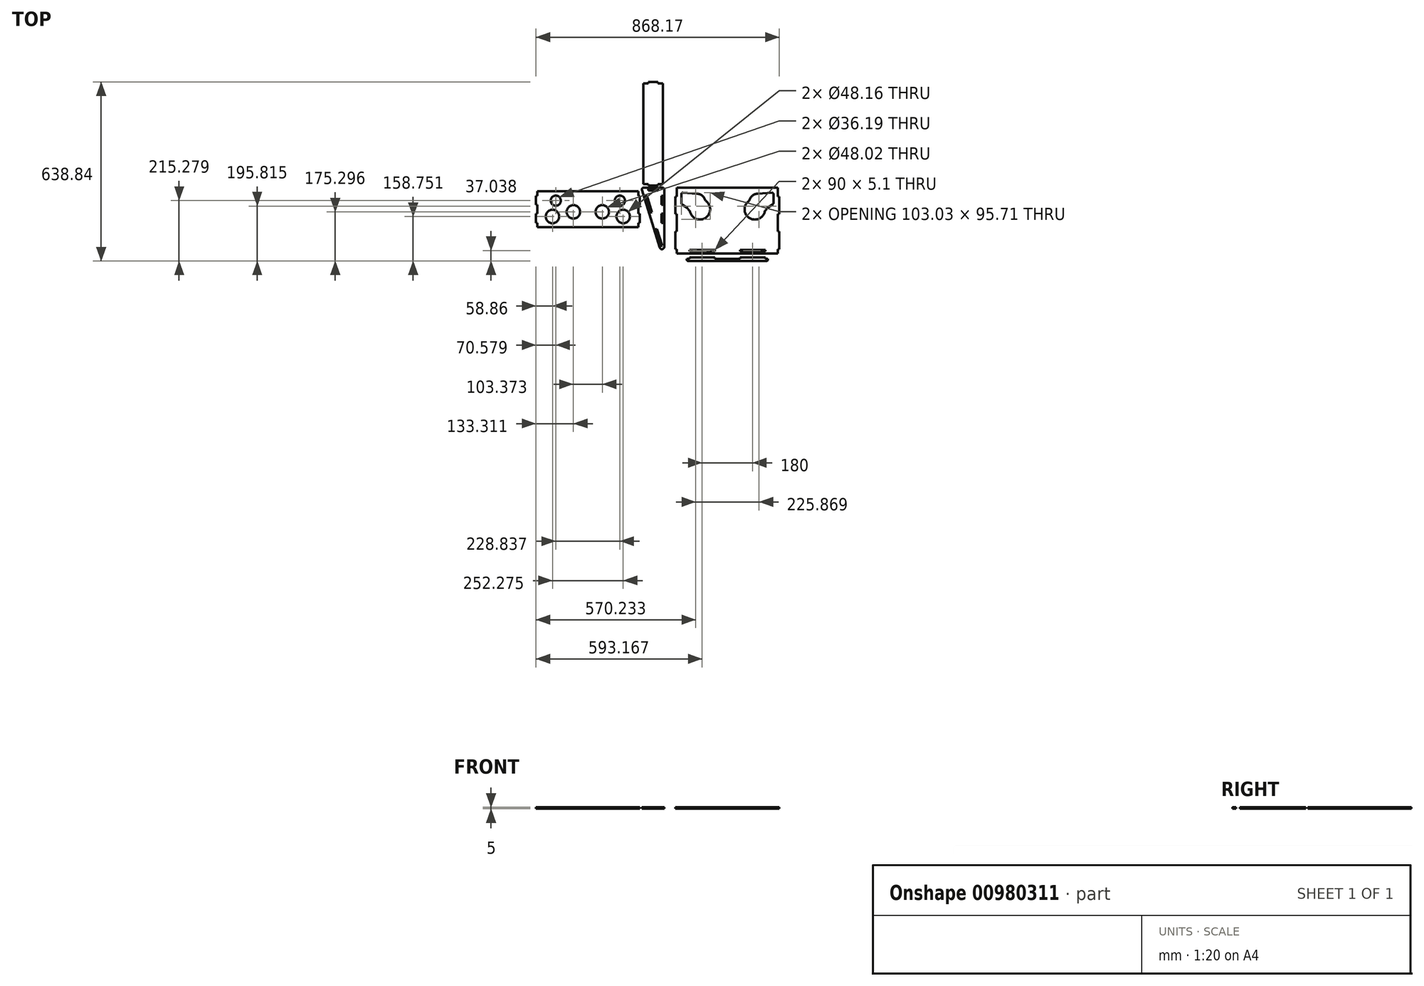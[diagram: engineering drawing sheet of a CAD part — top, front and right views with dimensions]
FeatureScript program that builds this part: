
annotation { "Feature Type Name" : "Feature", "Feature Type Description" : "" }
export const myFeature = defineFeature(function(context is Context, id is Id, definition is map)
    precondition{}
    {
        {
            var Q0;
            Q0=qCreatedBy(makeId("Top.planeOp"),FACE);
            var sketch = newSketch(context, id + "F0", { "sketchPlane" : qUnion([Q0])});
            skLineSegment(sketch, "E0.1", {"start": v(-213.88, 114.6) * mm, "end": v(-213.88, 52.1) * mm});
            skLineSegment(sketch, "E1.0", {"start": v(-208.88, 145.84) * mm, "end": v(151.12, 145.84) * mm});
            skLineSegment(sketch, "E1.1", {"start": v(-208.88, 145.84) * mm, "end": v(-208.88, 114.6) * mm});
            skLineSegment(sketch, "E1.3", {"start": v(151.12, 145.84) * mm, "end": v(151.12, 114.6) * mm});
            skLineSegment(sketch, "E2", {"start": v(-208.88, 20.84) * mm, "end": v(-208.88, 52.1) * mm});
            skLineSegment(sketch, "E3", {"start": v(-208.88, 114.6) * mm, "end": v(-208.88, 145.84) * mm});
            skLineSegment(sketch, "E4", {"start": v(-208.88, 114.6) * mm, "end": v(-213.88, 114.6) * mm});
            skLineSegment(sketch, "E5.MirrorCS", {"start": v(-208.88, 52.1) * mm, "end": v(-213.88, 52.1) * mm});
            skLineSegment(sketch, "E6.MirrorCS", {"start": v(-208.88, -10.4) * mm, "end": v(-213.88, -10.4) * mm});
            skLineSegment(sketch, "E7.MirrorCS", {"start": v(-208.88, -72.9) * mm, "end": v(-213.88, -72.9) * mm});
            skLineSegment(sketch, "E8.trimOffspring", {"start": v(-213.88, -10.4) * mm, "end": v(-213.88, -72.9) * mm});
            skPoint(sketch, "E9.end.orphan", {"position": v(-213.88, 20.84) * mm});
            skPoint(sketch, "E0.0.start.orphan", {"position": v(-213.88, 150.84) * mm});
            skPoint(sketch, "E0.2.start.orphan", {"position": v(-213.88, -109.16) * mm});
            skLineSegment(sketch, "E10", {"start": v(-270.56, -67.1) * mm, "end": v(-333.63, 139.38) * mm});
            skLineSegment(sketch, "E11", {"start": v(-328.85, 145.84) * mm, "end": v(-259.1, 145.84) * mm});
            skLineSegment(sketch, "E12", {"start": v(-254.24, -65.88) * mm, "end": v(-254.24, 140.84) * mm});
            skLineSegment(sketch, "E13", {"start": v(-259.1, 145.84) * mm, "end": v(-259.24, 145.84) * mm});
            skLineSegment(sketch, "E14", {"start": v(-335.6, 145.84) * mm, "end": v(-326.48, 115.95) * mm});
            skLineSegment(sketch, "E15", {"start": v(-321.68, 117.42) * mm, "end": v(-303.43, 57.65) * mm});
            skLineSegment(sketch, "E16", {"start": v(-303.43, 57.65) * mm, "end": v(-298.55, 59.14) * mm});
            skLineSegment(sketch, "E17", {"start": v(-298.55, 59.14) * mm, "end": v(-316.8, 118.91) * mm});
            skLineSegment(sketch, "E18", {"start": v(-321.68, 117.42) * mm, "end": v(-316.8, 118.91) * mm});
            skLineSegment(sketch, "E19", {"start": v(-285.1, -2.1) * mm, "end": v(-266.8, -61.87) * mm});
            skLineSegment(sketch, "E20", {"start": v(-266.8, -61.87) * mm, "end": v(-261.93, -60.37) * mm});
            skLineSegment(sketch, "E21", {"start": v(-261.93, -60.37) * mm, "end": v(-280.22, -0.61) * mm});
            skLineSegment(sketch, "E22", {"start": v(-285.1, -2.1) * mm, "end": v(-280.22, -0.61) * mm});
            skPoint(sketch, "E23.orphan", {"position": v(-280.41, 0) * mm});
            skPoint(sketch, "E24.orphan", {"position": v(-208.88, 83.34) * mm});
            skLineSegment(sketch, "E25.trimOffspring", {"start": v(-208.88, 20.84) * mm, "end": v(-208.88, -10.4) * mm});
            skLineSegment(sketch, "E26.trimOffspring", {"start": v(-208.88, -72.9) * mm, "end": v(-208.88, -88.53) * mm});
            skPoint(sketch, "E27.visualSharp", {"position": v(-335.6, 145.84) * mm});
            skArc(sketch, "E27.filletArc", {"start": v(-328.85, 145.84) * mm, "mid": v(-332.87, 143.82) * mm, "end": v(-333.63, 139.38) * mm});
            skPoint(sketch, "E28.visualSharp", {"position": v(-254.24, 145.84) * mm});
            skArc(sketch, "E28.filletArc", {"start": v(-254.24, 140.84) * mm, "mid": v(-255.7, 144.38) * mm, "end": v(-259.24, 145.84) * mm});
            skLineSegment(sketch, "E29", {"start": v(-328.85, 158.63) * mm, "end": v(-311.41, 158.63) * mm});
            skLineSegment(sketch, "E30", {"start": v(-259.1, 158.63) * mm, "end": v(-259.1, 518.63) * mm});
            skLineSegment(sketch, "E31", {"start": v(-259.1, 518.63) * mm, "end": v(-276.53, 518.63) * mm});
            skLineSegment(sketch, "E32", {"start": v(-328.85, 518.63) * mm, "end": v(-328.85, 158.63) * mm});
            skLineSegment(sketch, "E33", {"start": v(-293.97, 153.63) * mm, "end": v(-311.41, 153.63) * mm});
            skLineSegment(sketch, "E34", {"start": v(-311.41, 153.63) * mm, "end": v(-311.41, 158.63) * mm});
            skLineSegment(sketch, "E35.MirrorCS", {"start": v(-276.53, 153.63) * mm, "end": v(-276.53, 158.63) * mm});
            skPoint(sketch, "E36.orphan", {"position": v(-328.85, 153.63) * mm});
            skLineSegment(sketch, "E37", {"start": v(-293.97, 153.63) * mm, "end": v(-276.53, 153.63) * mm});
            skLineSegment(sketch, "E38.trimOffspring", {"start": v(-276.53, 158.63) * mm, "end": v(-259.1, 158.63) * mm});
            skPoint(sketch, "E39.orphan", {"position": v(-293.97, 158.63) * mm});
            skLineSegment(sketch, "E40", {"start": v(-311.41, 140.84) * mm, "end": v(-276.53, 140.84) * mm});
            skLineSegment(sketch, "E41", {"start": v(-276.53, 140.84) * mm, "end": v(-276.53, 135.74) * mm});
            skLineSegment(sketch, "E42", {"start": v(-276.53, 135.74) * mm, "end": v(-311.41, 135.74) * mm});
            skLineSegment(sketch, "E43", {"start": v(-311.41, 135.74) * mm, "end": v(-311.41, 140.84) * mm});
            skPoint(sketch, "E44.start.orphan", {"position": v(-311.41, 145.84) * mm});
            skLineSegment(sketch, "E45", {"start": v(-259.24, 117.32) * mm, "end": v(-259.24, 85.2) * mm});
            skLineSegment(sketch, "E46", {"start": v(-264.34, 20.94) * mm, "end": v(-264.34, 53.07) * mm});
            skLineSegment(sketch, "E47", {"start": v(-264.34, 85.2) * mm, "end": v(-264.34, 117.32) * mm});
            skLineSegment(sketch, "E48", {"start": v(-264.34, 101.26) * mm, "end": v(-264.34, 117.32) * mm});
            skLineSegment(sketch, "E49", {"start": v(-264.34, 117.32) * mm, "end": v(-259.24, 117.32) * mm});
            skLineSegment(sketch, "E50.MirrorCS", {"start": v(-264.34, 85.2) * mm, "end": v(-259.24, 85.2) * mm});
            skLineSegment(sketch, "E51.MirrorCS", {"start": v(-264.34, 53.07) * mm, "end": v(-259.24, 53.07) * mm});
            skLineSegment(sketch, "E52.MirrorCS", {"start": v(-264.34, 20.94) * mm, "end": v(-259.24, 20.94) * mm});
            skPoint(sketch, "E53.end.orphan", {"position": v(-259.24, 69.13) * mm});
            skPoint(sketch, "E54.end.orphan", {"position": v(-259.24, 101.26) * mm});
            skLineSegment(sketch, "E55", {"start": v(-347.05, 133.38) * mm, "end": v(-347.05, 117.32) * mm});
            skLineSegment(sketch, "E56", {"start": v(-347.05, 4.88) * mm, "end": v(-707.05, 4.88) * mm});
            skLineSegment(sketch, "E57", {"start": v(-707.05, 4.88) * mm, "end": v(-707.05, 20.94) * mm});
            skLineSegment(sketch, "E58", {"start": v(-707.05, 133.38) * mm, "end": v(-347.05, 133.38) * mm});
            skPoint(sketch, "E59.end.orphan", {"position": v(-259.24, 133.38) * mm});
            skPoint(sketch, "E60.orphan", {"position": v(-264.34, 133.38) * mm});
            skPoint(sketch, "E61.orphan", {"position": v(-264.34, 69.13) * mm});
            skLineSegment(sketch, "E62.trimOffspring", {"start": v(-259.24, 53.07) * mm, "end": v(-259.24, 20.94) * mm});
            skPoint(sketch, "E63.end.orphan", {"position": v(-264.34, 4.88) * mm});
            skPoint(sketch, "E63.start.orphan", {"position": v(-259.24, 4.88) * mm});
            skLineSegment(sketch, "E64", {"start": v(-347.05, 85.2) * mm, "end": v(-342.05, 85.2) * mm});
            skLineSegment(sketch, "E65", {"start": v(-342.05, 85.2) * mm, "end": v(-342.05, 117.32) * mm});
            skLineSegment(sketch, "E66", {"start": v(-342.05, 117.32) * mm, "end": v(-347.05, 117.32) * mm});
            skLineSegment(sketch, "E67", {"start": v(-264.34, 69.13) * mm, "end": v(-259.24, 69.13) * mm});
            skLineSegment(sketch, "E68.MirrorCS", {"start": v(-342.05, 20.94) * mm, "end": v(-347.05, 20.94) * mm});
            skLineSegment(sketch, "E69.MirrorCS", {"start": v(-342.05, 53.07) * mm, "end": v(-342.05, 20.94) * mm});
            skLineSegment(sketch, "E70.MirrorCS", {"start": v(-347.05, 53.07) * mm, "end": v(-342.05, 53.07) * mm});
            skLineSegment(sketch, "E71.trimOffspring", {"start": v(-347.05, 85.2) * mm, "end": v(-347.05, 53.07) * mm});
            skLineSegment(sketch, "E72.trimOffspring", {"start": v(-347.05, 20.94) * mm, "end": v(-347.05, 4.88) * mm});
            skArc(sketch, "E73", {"start": v(-270.56, -67.1) * mm, "mid": v(-261.92, -72.98) * mm, "end": v(-254.24, -65.88) * mm});
            skLineSegment(sketch, "E74.MirrorCS", {"start": v(-707.05, 85.2) * mm, "end": v(-712.05, 85.2) * mm});
            skLineSegment(sketch, "E75.MirrorCS", {"start": v(-712.05, 117.32) * mm, "end": v(-707.05, 117.32) * mm});
            skLineSegment(sketch, "E76.MirrorCS", {"start": v(-707.05, 53.07) * mm, "end": v(-712.05, 53.07) * mm});
            skLineSegment(sketch, "E77.MirrorCS", {"start": v(-712.05, 20.94) * mm, "end": v(-707.05, 20.94) * mm});
            skLineSegment(sketch, "E78.MirrorCS", {"start": v(-707.05, 133.38) * mm, "end": v(-707.05, 117.32) * mm});
            skLineSegment(sketch, "E79.MirrorCS", {"start": v(-707.05, 20.94) * mm, "end": v(-707.05, 4.88) * mm});
            skLineSegment(sketch, "E80.MirrorCS", {"start": v(-712.05, 53.07) * mm, "end": v(-712.05, 20.94) * mm});
            skLineSegment(sketch, "E81.MirrorCS", {"start": v(-707.05, 85.2) * mm, "end": v(-707.05, 53.07) * mm});
            skPoint(sketch, "E82.MirrorP", {"position": v(-718.5, 145.84) * mm});
            skLineSegment(sketch, "E83.MirrorCS", {"start": v(-712.05, 85.2) * mm, "end": v(-712.05, 117.32) * mm});
            skLineSegment(sketch, "E84.trimOffspring", {"start": v(-707.05, 117.32) * mm, "end": v(-707.05, 133.38) * mm});
            skLineSegment(sketch, "E85.trimOffspring", {"start": v(-707.05, 53.07) * mm, "end": v(-707.05, 85.2) * mm});
            skPoint(sketch, "E86.start.orphan", {"position": v(-527.05, 133.38) * mm});
            skLineSegment(sketch, "E87", {"start": v(-208.88, -88.53) * mm, "end": v(151.12, -88.53) * mm});
            skPoint(sketch, "E1.2.start.orphan", {"position": v(-208.88, -104.16) * mm});
            skLineSegment(sketch, "E88.MirrorCS", {"start": v(156.12, -10.4) * mm, "end": v(156.12, -72.9) * mm});
            skLineSegment(sketch, "E89.MirrorCS", {"start": v(151.12, -72.9) * mm, "end": v(156.12, -72.9) * mm});
            skPoint(sketch, "E90.MirrorP", {"position": v(151.12, 83.34) * mm});
            skLineSegment(sketch, "E91.MirrorCS", {"start": v(151.12, -10.4) * mm, "end": v(156.12, -10.4) * mm});
            skLineSegment(sketch, "E92.MirrorCS", {"start": v(151.12, 20.84) * mm, "end": v(151.12, 52.1) * mm});
            skLineSegment(sketch, "E93.MirrorCS", {"start": v(156.12, 114.6) * mm, "end": v(156.12, 52.1) * mm});
            skLineSegment(sketch, "E94.MirrorCS", {"start": v(151.12, 114.6) * mm, "end": v(156.12, 114.6) * mm});
            skLineSegment(sketch, "E95.MirrorCS", {"start": v(151.12, 52.1) * mm, "end": v(156.12, 52.1) * mm});
            skLineSegment(sketch, "E96.MirrorCS", {"start": v(151.12, 20.84) * mm, "end": v(151.12, -10.4) * mm});
            skLineSegment(sketch, "E97.trimOffspring", {"start": v(151.12, 52.1) * mm, "end": v(151.12, -10.4) * mm});
            skLineSegment(sketch, "E98.trimOffspring", {"start": v(151.12, -72.9) * mm, "end": v(151.12, -88.53) * mm});
            skPoint(sketch, "E99.start.orphan", {"position": v(-28.88, 145.84) * mm});
            skLineSegment(sketch, "E100.MirrorCS", {"start": v(-293.97, 523.63) * mm, "end": v(-311.41, 523.63) * mm});
            skLineSegment(sketch, "E101.MirrorCS", {"start": v(-293.97, 523.63) * mm, "end": v(-276.53, 523.63) * mm});
            skLineSegment(sketch, "E102.MirrorCS", {"start": v(-276.53, 523.63) * mm, "end": v(-276.53, 518.63) * mm});
            skLineSegment(sketch, "E103.MirrorCS", {"start": v(-311.41, 523.63) * mm, "end": v(-311.41, 518.63) * mm});
            skLineSegment(sketch, "E104.trimOffspring", {"start": v(-311.41, 518.63) * mm, "end": v(-328.85, 518.63) * mm});
            skPoint(sketch, "E105.start.orphan", {"position": v(-328.85, 338.63) * mm});
            skCircle(sketch, "E106", {"center": v(-641.47, 100.07) * mm, "radius": 18.1 * mm});
            skCircle(sketch, "E107", {"center": v(-578.74, 60.09) * mm, "radius": 24 * mm});
            skCircle(sketch, "E108", {"center": v(-653.19, 43.54) * mm, "radius": 24.08 * mm});
            skLineSegment(sketch, "E109", {"start": v(-527.05, 133.38) * mm, "end": v(-527.05, 102.83) * mm});
            skCircle(sketch, "E110.MirrorC", {"center": v(-412.63, 100.07) * mm, "radius": 18.1 * mm});
            skCircle(sketch, "E111.MirrorC", {"center": v(-400.91, 43.54) * mm, "radius": 24.08 * mm});
            skCircle(sketch, "E112.MirrorC", {"center": v(-475.37, 60.09) * mm, "radius": 24 * mm});
            skLineSegment(sketch, "E113", {"start": v(-208.88, -88.53) * mm, "end": v(-208.88, -80.72) * mm});
            skLineSegment(sketch, "E114", {"start": v(-163.88, -80.72) * mm, "end": v(-73.88, -80.72) * mm});
            skLineSegment(sketch, "E115", {"start": v(-28.88, -80.72) * mm, "end": v(-28.88, -75.62) * mm});
            skLineSegment(sketch, "E116", {"start": v(-73.88, -75.62) * mm, "end": v(-163.88, -75.62) * mm});
            skLineSegment(sketch, "E117", {"start": v(-118.88, -80.72) * mm, "end": v(-73.88, -80.72) * mm});
            skLineSegment(sketch, "E118", {"start": v(-73.88, -80.72) * mm, "end": v(-73.88, -75.62) * mm});
            skLineSegment(sketch, "E119.MirrorCS", {"start": v(-163.88, -80.72) * mm, "end": v(-163.88, -75.62) * mm});
            skLineSegment(sketch, "E120.MirrorCS", {"start": v(16.12, -80.72) * mm, "end": v(16.12, -75.62) * mm});
            skLineSegment(sketch, "E121.MirrorCS", {"start": v(106.12, -80.72) * mm, "end": v(106.12, -75.62) * mm});
            skPoint(sketch, "E122.start.orphan", {"position": v(-118.88, -75.62) * mm});
            skPoint(sketch, "E123.orphan", {"position": v(-208.88, -75.62) * mm});
            skLineSegment(sketch, "E124.trimOffspring", {"start": v(16.12, -80.72) * mm, "end": v(106.12, -80.72) * mm});
            skPoint(sketch, "E125.orphan", {"position": v(151.12, -80.72) * mm});
            skLineSegment(sketch, "E126", {"start": v(16.12, -75.62) * mm, "end": v(106.12, -75.62) * mm});
            skLineSegment(sketch, "E127", {"start": v(-163.88, -102.2) * mm, "end": v(-73.88, -102.2) * mm});
            skLineSegment(sketch, "E128", {"start": v(106.12, -102.2) * mm, "end": v(106.12, -107.2) * mm});
            skLineSegment(sketch, "E129", {"start": v(106.12, -107.2) * mm, "end": v(116.12, -107.2) * mm});
            skLineSegment(sketch, "E130", {"start": v(116.12, -107.2) * mm, "end": v(116.12, -110.2) * mm});
            skLineSegment(sketch, "E131.MirrorCS", {"start": v(-163.88, -102.2) * mm, "end": v(-163.88, -107.2) * mm});
            skLineSegment(sketch, "E132.MirrorCS", {"start": v(-163.88, -107.2) * mm, "end": v(-173.88, -107.2) * mm});
            skLineSegment(sketch, "E133.MirrorCS", {"start": v(-173.88, -107.2) * mm, "end": v(-173.88, -110.2) * mm});
            skLineSegment(sketch, "E134", {"start": v(-168.88, -115.2) * mm, "end": v(111.12, -115.2) * mm});
            skLineSegment(sketch, "E135", {"start": v(-73.88, -102.2) * mm, "end": v(-73.88, -107.2) * mm});
            skLineSegment(sketch, "E136", {"start": v(-73.88, -107.2) * mm, "end": v(16.12, -107.2) * mm});
            skLineSegment(sketch, "E137", {"start": v(16.12, -107.2) * mm, "end": v(16.12, -102.2) * mm});
            skLineSegment(sketch, "E138.trimOffspring", {"start": v(16.12, -102.2) * mm, "end": v(106.12, -102.2) * mm});
            skLineSegment(sketch, "E139.bottom", {"start": v(65.05, -133.52) * mm, "end": v(81.29, -133.52) * mm});
            skLineSegment(sketch, "E139.top", {"start": v(65.05, -151.69) * mm, "end": v(86.29, -151.69) * mm});
            skLineSegment(sketch, "E139.left", {"start": v(65.05, -133.52) * mm, "end": v(65.05, -151.69) * mm});
            skLineSegment(sketch, "E139.right", {"start": v(86.29, -138.52) * mm, "end": v(86.29, -151.69) * mm});
            skPoint(sketch, "E140.visualSharp", {"position": v(86.29, -133.52) * mm});
            skArc(sketch, "E140.filletArc", {"start": v(86.29, -138.52) * mm, "mid": v(84.82, -134.99) * mm, "end": v(81.29, -133.52) * mm});
            skPoint(sketch, "E141.visualSharp", {"position": v(116.12, -115.2) * mm});
            skArc(sketch, "E141.filletArc", {"start": v(111.12, -115.2) * mm, "mid": v(114.65, -113.74) * mm, "end": v(116.12, -110.2) * mm});
            skPoint(sketch, "E142.visualSharp", {"position": v(-173.88, -115.2) * mm});
            skArc(sketch, "E142.filletArc", {"start": v(-173.88, -110.2) * mm, "mid": v(-172.42, -113.74) * mm, "end": v(-168.88, -115.2) * mm});
            skArc(sketch, "E143", {"start": v(-171.34, 73.41) * mm, "mid": v(-167.7, 68.02) * mm, "end": v(-163.1, 63.4) * mm});
            skLineSegment(sketch, "E144", {"start": v(-171.34, 73.41) * mm, "end": v(-191.2, 87.33) * mm});
            skLineSegment(sketch, "E145", {"start": v(-193.33, 91.42) * mm, "end": v(-193.33, 123.47) * mm});
            skLineSegment(sketch, "E146", {"start": v(-188.02, 128.46) * mm, "end": v(-138.38, 125.34) * mm});
            skPoint(sketch, "E147.visualSharp", {"position": v(-193.33, 128.8) * mm});
            skArc(sketch, "E147.filletArc", {"start": v(-188.02, 128.46) * mm, "mid": v(-191.76, 127.11) * mm, "end": v(-193.33, 123.47) * mm});
            skPoint(sketch, "E148.visualSharp", {"position": v(-193.33, 88.82) * mm});
            skArc(sketch, "E148.filletArc", {"start": v(-193.33, 91.42) * mm, "mid": v(-192.77, 89.12) * mm, "end": v(-191.2, 87.33) * mm});
            skArc(sketch, "E149.MirrorCS", {"start": v(135.57, 91.42) * mm, "mid": v(135, 89.12) * mm, "end": v(133.44, 87.33) * mm});
            skArc(sketch, "E150.MirrorCS", {"start": v(130.25, 128.46) * mm, "mid": v(134, 127.11) * mm, "end": v(135.57, 123.47) * mm});
            skPoint(sketch, "E151.MirrorP", {"position": v(135.57, 128.8) * mm});
            skArc(sketch, "E152.MirrorCS", {"start": v(113.58, 73.41) * mm, "mid": v(109.93, 68.02) * mm, "end": v(105.34, 63.4) * mm});
            skLineSegment(sketch, "E153.MirrorCS", {"start": v(130.25, 128.46) * mm, "end": v(80.62, 125.34) * mm});
            skLineSegment(sketch, "E154.MirrorCS", {"start": v(113.58, 73.41) * mm, "end": v(133.44, 87.33) * mm});
            skPoint(sketch, "E155.MirrorP", {"position": v(135.57, 88.82) * mm});
            skLineSegment(sketch, "E156.MirrorCS", {"start": v(135.57, 91.42) * mm, "end": v(135.57, 123.47) * mm});
            skArc(sketch, "E157", {"start": v(-163.1, 63.4) * mm, "mid": v(-107, 38.53) * mm, "end": v(-106.81, 99.9) * mm});
            skArc(sketch, "E158.trimOffspring", {"start": v(-106.81, 99.9) * mm, "mid": v(-118.55, 117.64) * mm, "end": v(-138.38, 125.34) * mm});
            skArc(sketch, "E159.MirrorCS", {"start": v(105.34, 63.4) * mm, "mid": v(49.24, 38.53) * mm, "end": v(49.05, 99.9) * mm});
            skArc(sketch, "E160.trimOffspring", {"start": v(49.05, 99.9) * mm, "mid": v(60.79, 117.64) * mm, "end": v(80.62, 125.34) * mm});
            skSolve(sketch);
        }
        {
            var Q0;
            {var subQ1=sQuery(id+"F0.wireOp",EDGE,"E55");Q0=makeQuery(id+"F0.imprint","IMPRINT",FACE,{"disambiguationData":[TD([[makeQuery(id+"F0.imprint","IMPRINT",EDGE,{"derivedFrom":subQ1}),-1.0]])]});}
            var Q1;
            Q1=makeQuery(id+"F0.imprint","IMPRINT",FACE,{"disambiguationData":[TD([[makeQuery(id+"F0.imprint","IMPRINT",EDGE,{"derivedFrom":sQuery(id+"F0.wireOp",EDGE,"E29")}),1.0]])]});
            var Q2;
            Q2=makeQuery(id+"F0.imprint","IMPRINT",FACE,{"disambiguationData":[TD([[makeQuery(id+"F0.imprint","IMPRINT",EDGE,{"derivedFrom":sQuery(id+"F0.wireOp",EDGE,"E0.1")}),1.0]])]});
            var Q3;
            {var subQ2=sQuery(id+"F0.wireOp",EDGE,"E10");Q3=makeQuery(id+"F0.imprint","IMPRINT",FACE,{"disambiguationData":[TD([[makeQuery(id+"F0.imprint","IMPRINT",EDGE,{"derivedFrom":subQ2}),-1.0]])]});}
            var Q4;
            Q4=makeQuery(id+"F0.imprint","IMPRINT",FACE,{"disambiguationData":[TD([[makeQuery(id+"F0.imprint","IMPRINT",EDGE,{"derivedFrom":sQuery(id+"F0.wireOp",EDGE,"E127")}),-1.0]])]});
            extrude(context, id + "F1", {"entities" : qUnion([Q0, Q1, Q2, Q3, Q4]), "depth" : 5 * mm, "offsetDistance" : 25 * mm});
        }
    });
